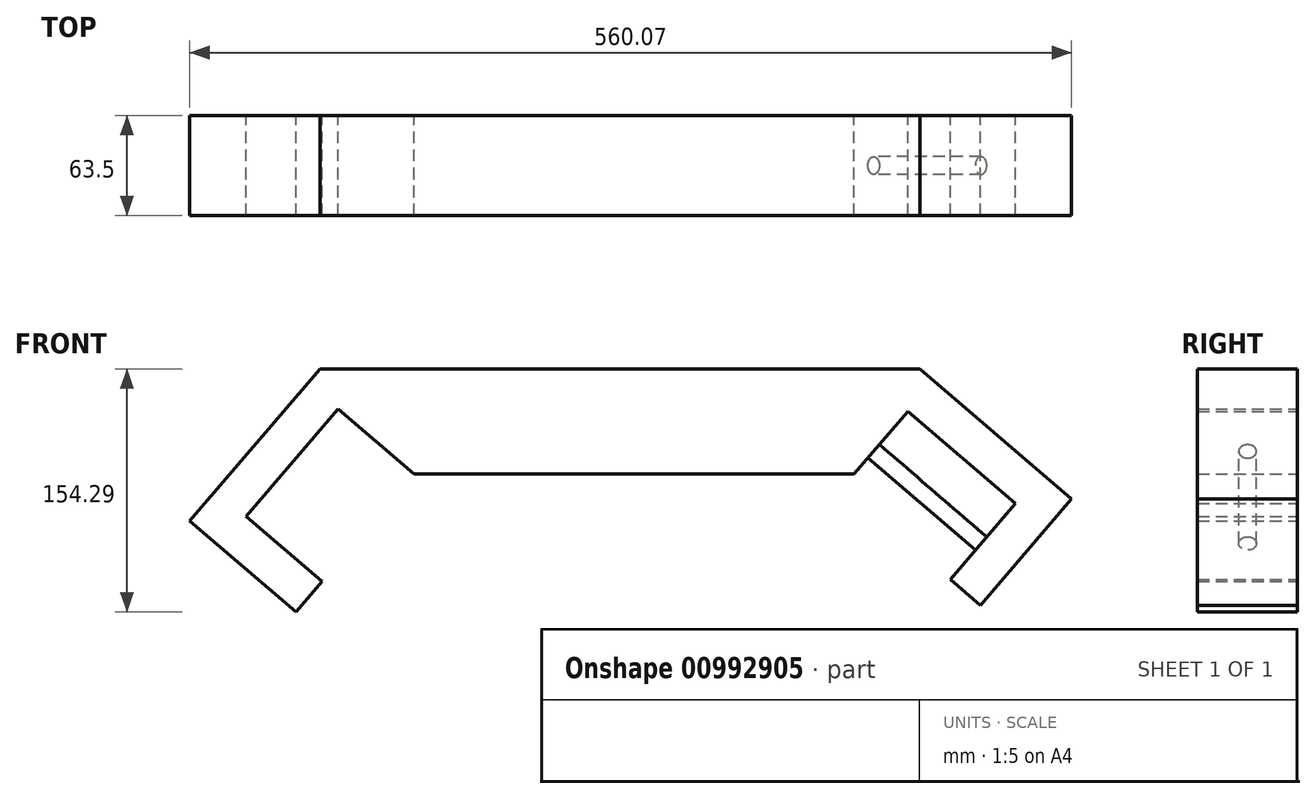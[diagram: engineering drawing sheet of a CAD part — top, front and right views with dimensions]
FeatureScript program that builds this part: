
annotation { "Feature Type Name" : "Feature", "Feature Type Description" : "" }
export const myFeature = defineFeature(function(context is Context, id is Id, definition is map)
    precondition{}
    {
        {
            var Q0;
            Q0=qCreatedBy(makeId("Front.planeOp"),FACE);
            var sketch = newSketch(context, id + "F0", { "sketchPlane" : qUnion([Q0])});
            skLineSegment(sketch, "E0", {"start": v(-35.81, 25.1) * mm, "end": v(46.82, 121.53) * mm});
            skLineSegment(sketch, "E1", {"start": v(46.82, 121.53) * mm, "end": v(427.82, 121.53) * mm});
            skLineSegment(sketch, "E2", {"start": v(427.82, 121.53) * mm, "end": v(524.26, 38.89) * mm});
            skLineSegment(sketch, "E3", {"start": v(524.26, 38.89) * mm, "end": v(466.41, -28.62) * mm});
            skLineSegment(sketch, "E4", {"start": v(466.41, -28.62) * mm, "end": v(447.12, -12.1) * mm});
            skLineSegment(sketch, "E5", {"start": v(447.12, -12.1) * mm, "end": v(488.44, 36.13) * mm});
            skLineSegment(sketch, "E6", {"start": v(488.44, 36.13) * mm, "end": v(420.23, 94.59) * mm});
            skLineSegment(sketch, "E7", {"start": v(420.23, 94.59) * mm, "end": v(378.9, 46.37) * mm});
            skLineSegment(sketch, "E8", {"start": v(-35.81, 25.1) * mm, "end": v(31.69, -32.76) * mm});
            skLineSegment(sketch, "E9", {"start": v(31.69, -32.76) * mm, "end": v(48.22, -13.47) * mm});
            skLineSegment(sketch, "E10", {"start": v(48.22, -13.47) * mm, "end": v(0, 27.85) * mm});
            skLineSegment(sketch, "E11", {"start": v(0, 27.85) * mm, "end": v(58.46, 96.07) * mm});
            skLineSegment(sketch, "E12", {"start": v(58.46, 96.07) * mm, "end": v(106.68, 54.75) * mm});
            skLineSegment(sketch, "E13", {"start": v(106.68, 54.75) * mm, "end": v(386.09, 54.75) * mm});
            skSolve(sketch);
        }
        {
            var Q0;
            Q0=makeQuery(id+"F0.imprint","IMPRINT",FACE,{"disambiguationData":[TD([[makeQuery(id+"F0.imprint","IMPRINT",EDGE,{"derivedFrom":sQuery(id+"F0.wireOp",EDGE,"E0")}),-1.0]])]});
            extrude(context, id + "F1", {"entities" : qUnion([Q0]), "depth" : 63.5 * mm, "offsetDistance" : 25.4 * mm});
        }
        {
            var Q0;
            Q0=makeQuery(id+"F1.opExtrude","SWEPT_FACE",FACE,{"disambiguationData":[OSD([sQuery(id+"F0.wireOp",EDGE,"E7")])]});
            var sketch = newSketch(context, id + "F2", { "sketchPlane" : qUnion([Q0])});
            skCircle(sketch, "E14", {"center": v(-31.75, 311.85) * mm, "radius": 5.61 * mm});
            skSolve(sketch);
        }
        {
            var Q0;
            Q0=makeQuery(id+"F2.imprint","IMPRINT",FACE,{"disambiguationData":[TD([[makeQuery(id+"F2.imprint","IMPRINT",EDGE,{"derivedFrom":sQuery(id+"F2.wireOp",EDGE,"E14")}),1.0]])]});
            extrude(context, id + "F3", {"entities" : qUnion([Q0]), "operationType" : NewBodyOperationType.ADD, "depth" : 107.7 * mm, "offsetDistance" : 25.4 * mm});
        }
        {
            var Q0;
            Q0=makeQuery(id+"F1.opExtrude","SWEPT_FACE",FACE,{"disambiguationData":[OSD([sQuery(id+"F0.wireOp",EDGE,"E12")])]});
            var sketch = newSketch(context, id + "F4", { "sketchPlane" : qUnion([Q0])});
            skCircle(sketch, "E15", {"center": v(26.33, 31.75) * mm, "radius": 6.1 * mm});
            skSolve(sketch);
        }
        {
            var Q0;
            Q0=sQuery(id+"F4.wireOp",EDGE,"E15");
            extrude(context, id + "F5", {"bodyType" : ToolBodyType.SURFACE, "surfaceEntities" : qUnion([Q0]), "depth" : 90.17 * mm, "offsetDistance" : 25.4 * mm});
        }
    });
